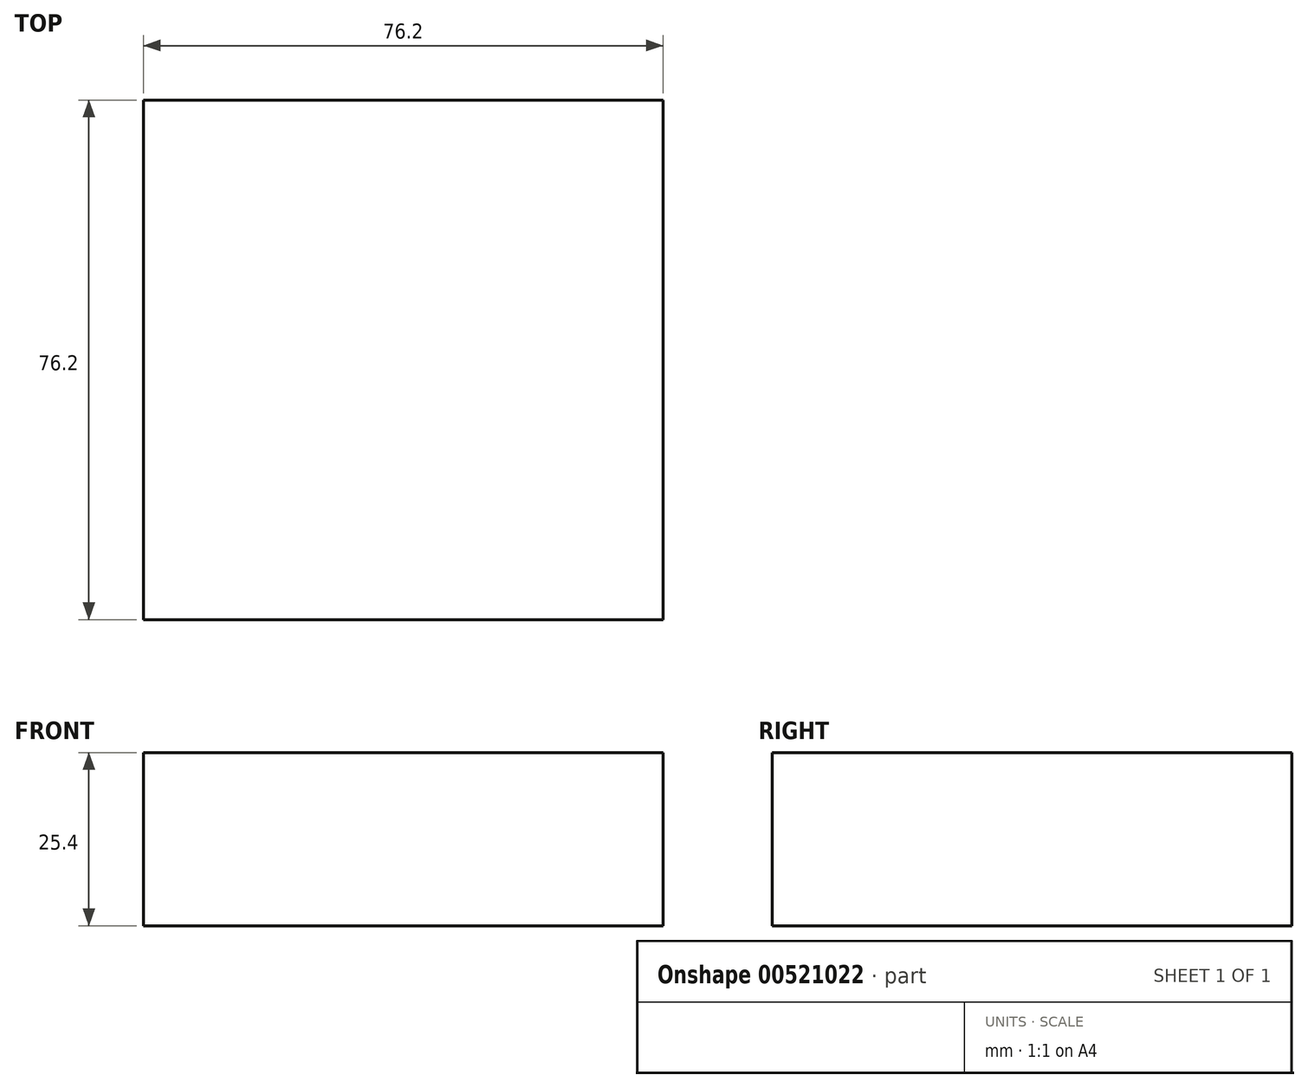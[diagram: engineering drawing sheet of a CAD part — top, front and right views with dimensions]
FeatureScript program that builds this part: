
annotation { "Feature Type Name" : "Feature", "Feature Type Description" : "" }
export const myFeature = defineFeature(function(context is Context, id is Id, definition is map)
    precondition{}
    {
        {
            var Q0;
            Q0=qCreatedBy(makeId("Top.planeOp"),FACE);
            var sketch = newSketch(context, id + "F0", { "sketchPlane" : qUnion([Q0])});
            skLineSegment(sketch, "E0.bottom", {"start": v(-25.4, 28.65) * mm, "end": v(50.8, 28.65) * mm});
            skLineSegment(sketch, "E0.top", {"start": v(-25.4, -47.55) * mm, "end": v(50.8, -47.55) * mm});
            skLineSegment(sketch, "E0.left", {"start": v(-25.4, 28.65) * mm, "end": v(-25.4, -47.55) * mm});
            skLineSegment(sketch, "E0.right", {"start": v(50.8, 28.65) * mm, "end": v(50.8, -47.55) * mm});
            skSolve(sketch);
        }
        {
            var Q0;
            Q0=makeQuery(id+"F0.imprint","IMPRINT",FACE,{"disambiguationData":[TD([[makeQuery(id+"F0.imprint","IMPRINT",EDGE,{"derivedFrom":sQuery(id+"F0.wireOp",EDGE,"E0.bottom")}),-1.0]])]});
            extrude(context, id + "F1", {"entities" : qUnion([Q0]), "depth" : 25.4 * mm, "offsetDistance" : 25.4 * mm});
        }
    });
